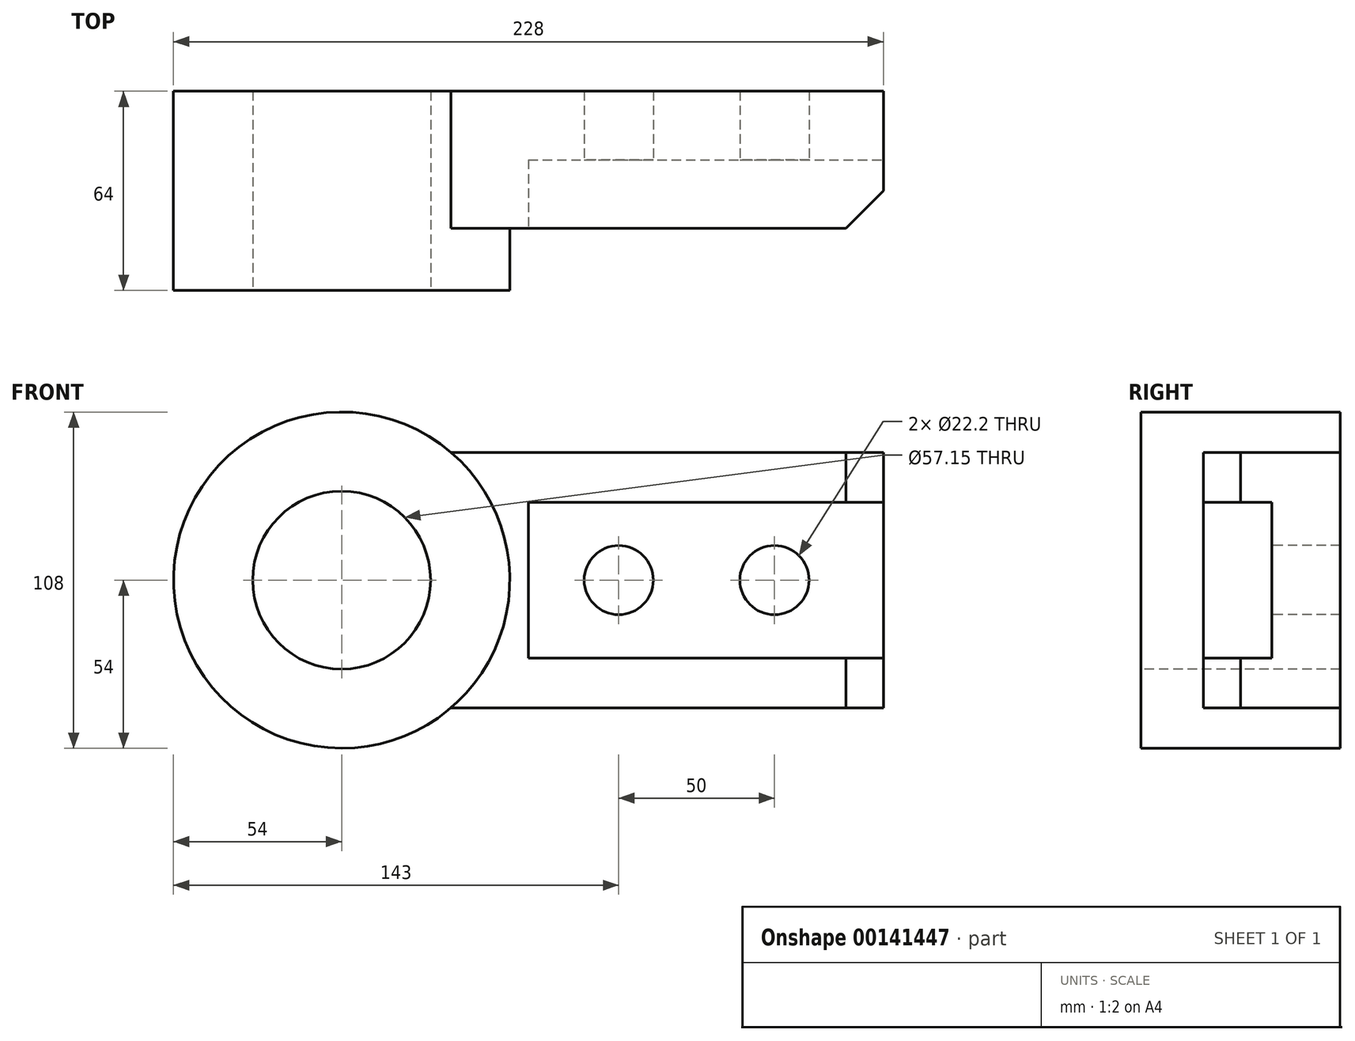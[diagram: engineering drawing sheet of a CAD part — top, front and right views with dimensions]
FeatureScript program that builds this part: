
annotation { "Feature Type Name" : "Feature", "Feature Type Description" : "" }
export const myFeature = defineFeature(function(context is Context, id is Id, definition is map)
    precondition{}
    {
        {
            var Q0;
            Q0=qCreatedBy(makeId("Front.planeOp"),FACE);
            var sketch = newSketch(context, id + "F0", { "sketchPlane" : qUnion([Q0])});
            skCircle(sketch, "E0", {"center": v(0, 0) * mm, "radius": 28.58 * mm});
            skLineSegment(sketch, "E1", {"start": v(0, 82) * mm, "end": v(0, 0) * mm});
            skCircle(sketch, "E2", {"center": v(0, 0) * mm, "radius": 54 * mm});
            skLineSegment(sketch, "E3", {"start": v(0, 0) * mm, "end": v(174, 0) * mm});
            skLineSegment(sketch, "E4", {"start": v(174, 0) * mm, "end": v(174, -41) * mm});
            skLineSegment(sketch, "E5", {"start": v(174, 0) * mm, "end": v(174, 41) * mm});
            skLineSegment(sketch, "E6", {"start": v(174, -41) * mm, "end": v(0, -41) * mm});
            skLineSegment(sketch, "E7", {"start": v(0, -41) * mm, "end": v(0, 0) * mm});
            skLineSegment(sketch, "E8", {"start": v(174, 41) * mm, "end": v(0, 41) * mm});
            skLineSegment(sketch, "E9", {"start": v(0, 41) * mm, "end": v(0, 0) * mm});
            skSolve(sketch);
        }
        {
            var Q0;
            {var subQ5=sQuery(id+"F0.wireOp",EDGE,"E5");Q0=makeQuery(id+"F0.imprint","IMPRINT",FACE,{"disambiguationData":[TD([[makeQuery(id+"F0.imprint","IMPRINT",EDGE,{"derivedFrom":subQ5}),1.0]])]});}
            var Q1;
            {var subQ5=sQuery(id+"F0.wireOp",EDGE,"E4");Q1=makeQuery(id+"F0.imprint","IMPRINT",FACE,{"disambiguationData":[TD([[makeQuery(id+"F0.imprint","IMPRINT",EDGE,{"derivedFrom":subQ5}),-1.0]])]});}
            extrude(context, id + "F1", {"entities" : qUnion([Q0, Q1]), "depth" : 44 * mm});
        }
        {
            var Q0;
            Q0=qCreatedBy(makeId("Front.planeOp"),FACE);
            var sketch = newSketch(context, id + "F2", { "sketchPlane" : qUnion([Q0])});
            skCircle(sketch, "E10", {"center": v(0, 0) * mm, "radius": 54 * mm});
            skCircle(sketch, "E11", {"center": v(0, 0) * mm, "radius": 28.57 * mm});
            skSolve(sketch);
        }
        {
            var Q0;
            Q0=makeQuery(id+"F2.imprint","IMPRINT",FACE,{"disambiguationData":[TD([[makeQuery(id+"F2.imprint","IMPRINT",EDGE,{"derivedFrom":sQuery(id+"F2.wireOp",EDGE,"E10")}),1.0]])]});
            var Q1;
            Q1=makeQuery(id+"F2.imprint","IMPRINT",FACE,{"disambiguationData":[TD([[makeQuery(id+"F2.imprint","IMPRINT",EDGE,{"derivedFrom":sQuery(id+"F2.wireOp",EDGE,"E11")}),1.0]])]});
            extrude(context, id + "F3", {"entities" : qUnion([Q0, Q1]), "operationType" : NewBodyOperationType.ADD, "depth" : 64 * mm});
        }
        {
            var Q0;
            Q0=makeQuery(id+"F1.opExtrude","CAP_FACE",FACE,{"disambiguationData":[OSD([sQuery(id+"F0.wireOp",EDGE,"E2"),sQuery(id+"F0.wireOp",EDGE,"E4"),sQuery(id+"F0.wireOp",EDGE,"E5"),sQuery(id+"F0.wireOp",EDGE,"E6"),sQuery(id+"F0.wireOp",EDGE,"E8")])],"isStart":false});
            var sketch = newSketch(context, id + "F4", { "sketchPlane" : qUnion([Q0])});
            skLineSegment(sketch, "E12", {"start": v(174, -41) * mm, "end": v(60, -41) * mm});
            skLineSegment(sketch, "E13", {"start": v(60, -41) * mm, "end": v(60, -25) * mm});
            skLineSegment(sketch, "E14", {"start": v(60, -25) * mm, "end": v(174, -25) * mm});
            skLineSegment(sketch, "E15", {"start": v(174, 41) * mm, "end": v(60, 41) * mm});
            skLineSegment(sketch, "E16", {"start": v(60, 41) * mm, "end": v(60, 25) * mm});
            skLineSegment(sketch, "E17", {"start": v(60, 25) * mm, "end": v(174, 25) * mm});
            skLineSegment(sketch, "E18.bottom", {"start": v(60, 25) * mm, "end": v(60, 25) * mm});
            skLineSegment(sketch, "E18.top", {"start": v(60, -25) * mm, "end": v(60, -25) * mm});
            skLineSegment(sketch, "E19.bottom", {"start": v(174, -25) * mm, "end": v(60, -25) * mm});
            skLineSegment(sketch, "E19.top", {"start": v(174, 25) * mm, "end": v(60, 25) * mm});
            skLineSegment(sketch, "E19.left", {"start": v(174, -25) * mm, "end": v(174, 25) * mm});
            skLineSegment(sketch, "E19.right", {"start": v(60, -25) * mm, "end": v(60, 25) * mm});
            skSolve(sketch);
        }
        {
            var Q0;
            Q0 = qSketchRegion(id + "F4", true);
            extrude(context, id + "F5", {"entities" : qUnion([Q0]), "operationType" : NewBodyOperationType.REMOVE, "oppositeDirection" : true, "depth" : 22 * mm});
        }
        {
            var Q0;
            Q0=makeQuery(id+"F5.boolean.opBoolean","COPY",FACE,{"derivedFrom":makeQuery(id+"F5.opExtrude","CAP_FACE",FACE,{"disambiguationData":[OSD([sQuery(id+"F4.wireOp",EDGE,"E19.bottom"),sQuery(id+"F4.wireOp",EDGE,"E19.top"),sQuery(id+"F4.wireOp",EDGE,"E19.left"),sQuery(id+"F4.wireOp",EDGE,"E19.right")])],"isStart":false})});
            var sketch = newSketch(context, id + "F6", { "sketchPlane" : qUnion([Q0])});
            skLineSegment(sketch, "E20", {"start": v(174, -25) * mm, "end": v(174, 0) * mm});
            skLineSegment(sketch, "E21", {"start": v(174, 0) * mm, "end": v(139, 0) * mm});
            skLineSegment(sketch, "E22", {"start": v(139, 0) * mm, "end": v(89, 0) * mm});
            skCircle(sketch, "E23", {"center": v(89, 0) * mm, "radius": 11.1 * mm});
            skCircle(sketch, "E24", {"center": v(139, 0) * mm, "radius": 11.1 * mm});
            skSolve(sketch);
        }
        {
            var Q0;
            {var subQ0=sQuery(id+"F6.wireOp",EDGE,"E22");var subQ1=sQuery(id+"F6.wireOp",EDGE,"E21");var subQ2=makeQuery(id+"F6.imprint","INTERSECT",VERTEX,{"derivedFrom":[subQ1,subQ0]});Q0=makeQuery(id+"F6.imprint","IMPRINT",FACE,{"disambiguationData":[TD([[makeQuery(id+"F6.imprint","IMPRINT",EDGE,{"disambiguationData":[TD([[subQ2,1.0]])],"derivedFrom":subQ1}),-1.0]])]});}
            var Q1;
            {var subQ0=sQuery(id+"F6.wireOp",EDGE,"E22");var subQ1=sQuery(id+"F6.wireOp",EDGE,"E21");var subQ2=makeQuery(id+"F6.imprint","INTERSECT",VERTEX,{"derivedFrom":[subQ1,subQ0]});Q1=makeQuery(id+"F6.imprint","IMPRINT",FACE,{"disambiguationData":[TD([[makeQuery(id+"F6.imprint","IMPRINT",EDGE,{"disambiguationData":[TD([[subQ2,1.0]])],"derivedFrom":subQ1}),1.0]])]});}
            var Q2;
            Q2=makeQuery(id+"F6.imprint","IMPRINT",FACE,{"disambiguationData":[TD([[makeQuery(id+"F6.imprint","IMPRINT",EDGE,{"derivedFrom":sQuery(id+"F6.wireOp",EDGE,"E23")}),1.0]])]});
            extrude(context, id + "F7", {"entities" : qUnion([Q0, Q1, Q2]), "operationType" : NewBodyOperationType.REMOVE, "endBound" : BoundingType.THROUGH_ALL, "oppositeDirection" : true, "depth" : 25 * mm});
        }
        {
            var Q0;
            Q0=makeQuery(id+"F3.opExtrude","CAP_FACE",FACE,{"disambiguationData":[OSD([sQuery(id+"F2.wireOp",EDGE,"E10")])],"isStart":false});
            var sketch = newSketch(context, id + "F8", { "sketchPlane" : qUnion([Q0])});
            skCircle(sketch, "E25", {"center": v(0, 0) * mm, "radius": 28.57 * mm});
            skLineSegment(sketch, "E26", {"start": v(0, 0) * mm, "end": v(-54, 0) * mm});
            skSolve(sketch);
        }
        {
            var Q0;
            Q0=makeQuery(id+"F8.imprint","IMPRINT",FACE,{"disambiguationData":[TD([[makeQuery(id+"F8.imprint","IMPRINT",EDGE,{"derivedFrom":sQuery(id+"F8.wireOp",EDGE,"E25")}),1.0]])]});
            extrude(context, id + "F9", {"entities" : qUnion([Q0]), "operationType" : NewBodyOperationType.REMOVE, "endBound" : BoundingType.THROUGH_ALL, "oppositeDirection" : true, "depth" : 25 * mm});
        }
        {
            var Q0;
            Q0=makeQuery(id+"F1.opExtrude","SWEPT_FACE",FACE,{"disambiguationData":[OSD([sQuery(id+"F0.wireOp",EDGE,"E8")])]});
            var sketch = newSketch(context, id + "F10", { "sketchPlane" : qUnion([Q0])});
            skLineSegment(sketch, "E27", {"start": v(162, -44) * mm, "end": v(174, -32) * mm});
            skLineSegment(sketch, "E28", {"start": v(174, -32) * mm, "end": v(174, -44) * mm});
            skLineSegment(sketch, "E29", {"start": v(174, -44) * mm, "end": v(162, -44) * mm});
            skSolve(sketch);
        }
        {
            var Q0;
            Q0=makeQuery(id+"F10.imprint","IMPRINT",FACE,{"disambiguationData":[TD([[makeQuery(id+"F10.imprint","IMPRINT",EDGE,{"derivedFrom":sQuery(id+"F10.wireOp",EDGE,"E27")}),-1.0]])]});
            extrude(context, id + "F11", {"entities" : qUnion([Q0]), "operationType" : NewBodyOperationType.REMOVE, "endBound" : BoundingType.THROUGH_ALL, "oppositeDirection" : true, "depth" : 25 * mm});
        }
    });
